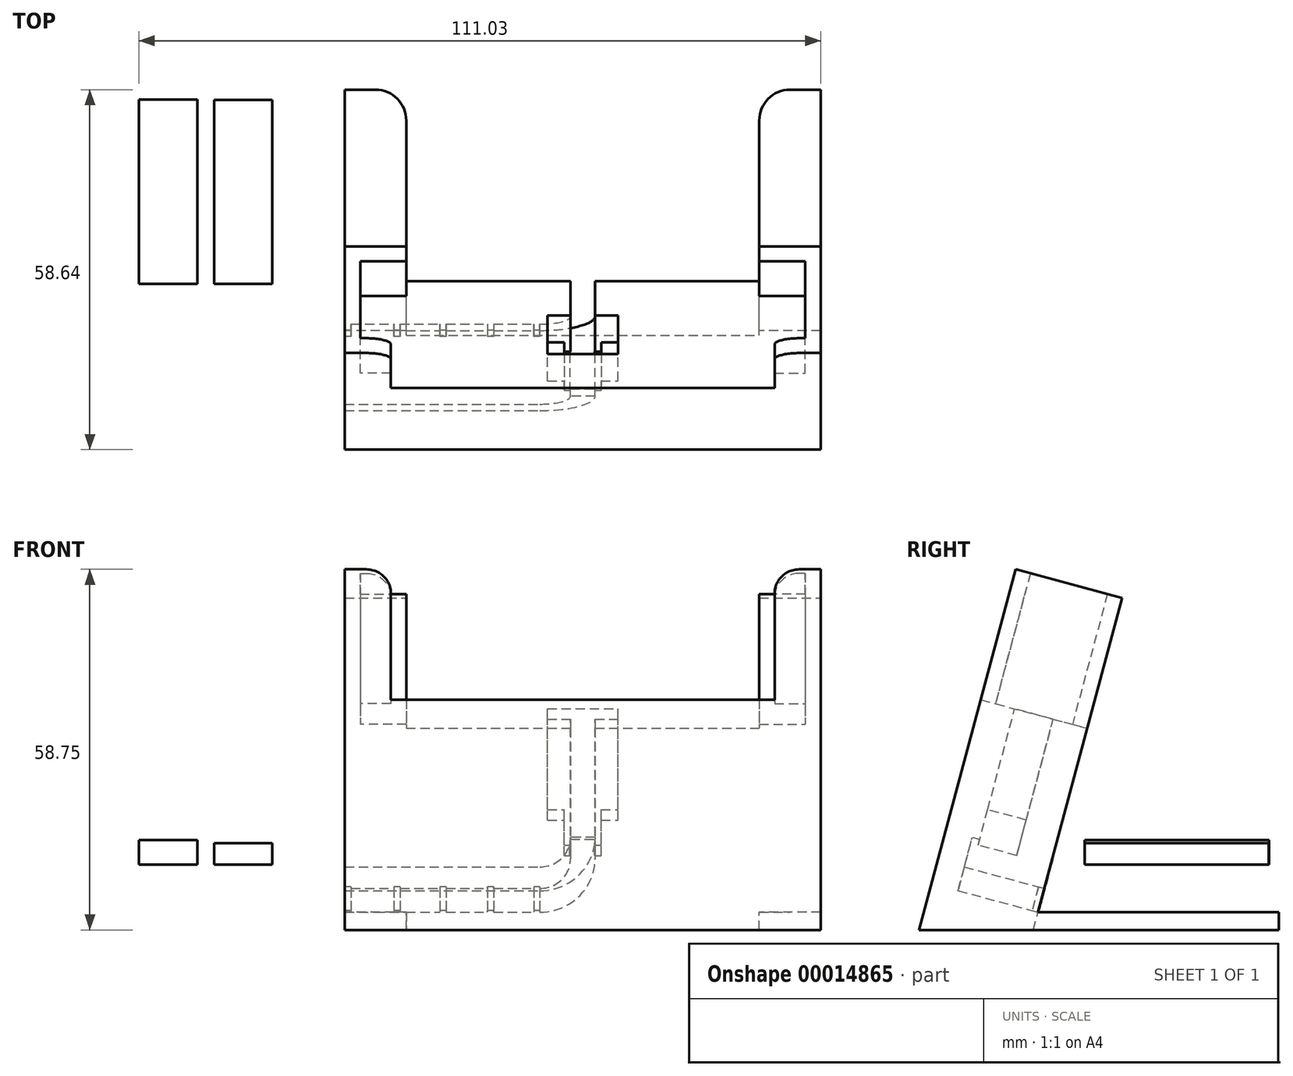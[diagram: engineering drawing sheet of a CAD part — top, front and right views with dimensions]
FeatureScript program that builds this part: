
annotation { "Feature Type Name" : "Feature", "Feature Type Description" : "" }
export const myFeature = defineFeature(function(context is Context, id is Id, definition is map)
    precondition{}
    {
        {
            var Q0;
            Q0=qCreatedBy(makeId("Top.planeOp"),FACE);
            var sketch = newSketch(context, id + "F0", { "sketchPlane" : qUnion([Q0])});
            skLineSegment(sketch, "E0.bottom", {"start": v(0, 0) * mm, "end": v(77.5, 0) * mm});
            skLineSegment(sketch, "E0.top", {"start": v(0, -18) * mm, "end": v(77.5, -18) * mm});
            skLineSegment(sketch, "E0.left", {"start": v(0, 0) * mm, "end": v(0, -18) * mm});
            skLineSegment(sketch, "E0.right", {"start": v(77.5, 0) * mm, "end": v(77.5, -18) * mm});
            skSolve(sketch);
        }
        {
            var Q0;
            Q0 = qSketchRegion(id + "F0", true);
            var Q1;
            Q1 = qSketchRegion(id + "F4", true);
            var Q2;
            Q2 = qSketchRegion(id + "F2", true);
            extrude(context, id + "F1", {"entities" : qUnion([Q0, Q1, Q2]), "depth" : 3 * mm, "hasSecondDirection" : true, "secondDirectionOppositeDirection" : true, "secondDirectionDepth" : 31 * mm});
        }
        {
            var Q0;
            Q0=makeQuery(id+"F0.imprint","IMPRINT",FACE,{"disambiguationData":[TD([[makeQuery(id+"F0.imprint","IMPRINT",EDGE,{"derivedFrom":sQuery(id+"F0.wireOp",EDGE,"E0.bottom")}),-1.0]])]});
            var sketch = newSketch(context, id + "F2", { "sketchPlane" : qUnion([Q0])});
            skLineSegment(sketch, "E1.bottom", {"start": v(0, 0) * mm, "end": v(10, 0) * mm});
            skLineSegment(sketch, "E1.top", {"start": v(0, -2.5) * mm, "end": v(10, -2.5) * mm});
            skLineSegment(sketch, "E1.left", {"start": v(0, 0) * mm, "end": v(0, -2.5) * mm});
            skLineSegment(sketch, "E1.right", {"start": v(10, 0) * mm, "end": v(10, -2.5) * mm});
            skLineSegment(sketch, "E2.bottom", {"start": v(0, -2.5) * mm, "end": v(2.5, -2.5) * mm});
            skLineSegment(sketch, "E2.top", {"start": v(0, -18) * mm, "end": v(2.5, -18) * mm});
            skLineSegment(sketch, "E2.left", {"start": v(0, -2.5) * mm, "end": v(0, -18) * mm});
            skLineSegment(sketch, "E2.right", {"start": v(2.5, -2.5) * mm, "end": v(2.5, -18) * mm});
            skLineSegment(sketch, "E3.bottom", {"start": v(2.5, -15.5) * mm, "end": v(7.5, -15.5) * mm});
            skLineSegment(sketch, "E3.top", {"start": v(2.5, -18) * mm, "end": v(7.5, -18) * mm});
            skLineSegment(sketch, "E3.left", {"start": v(2.5, -15.5) * mm, "end": v(2.5, -18) * mm});
            skLineSegment(sketch, "E3.right", {"start": v(7.5, -15.5) * mm, "end": v(7.5, -18) * mm});
            skLineSegment(sketch, "E4", {"start": v(38.75, 38.6) * mm, "end": v(38.75, -47.5) * mm});
            skLineSegment(sketch, "E5.0.MirrorCS", {"start": v(77.5, -2.5) * mm, "end": v(75, -2.5) * mm});
            skLineSegment(sketch, "E5.1.MirrorCS", {"start": v(77.5, -18) * mm, "end": v(75, -18) * mm});
            skLineSegment(sketch, "E5.2.MirrorCS", {"start": v(67.5, 0) * mm, "end": v(67.5, -2.5) * mm});
            skLineSegment(sketch, "E5.3.MirrorCS", {"start": v(77.5, 0) * mm, "end": v(77.5, -2.5) * mm});
            skLineSegment(sketch, "E5.4.MirrorCS", {"start": v(75, -15.5) * mm, "end": v(75, -18) * mm});
            skLineSegment(sketch, "E5.5.MirrorCS", {"start": v(70, -15.5) * mm, "end": v(70, -18) * mm});
            skLineSegment(sketch, "E5.6.MirrorCS", {"start": v(77.5, -2.5) * mm, "end": v(77.5, -18) * mm});
            skLineSegment(sketch, "E5.7.MirrorCS", {"start": v(77.5, 0) * mm, "end": v(67.5, 0) * mm});
            skLineSegment(sketch, "E5.8.MirrorCS", {"start": v(77.5, -2.5) * mm, "end": v(67.5, -2.5) * mm});
            skLineSegment(sketch, "E5.9.MirrorCS", {"start": v(75, -2.5) * mm, "end": v(75, -18) * mm});
            skLineSegment(sketch, "E5.10.MirrorCS", {"start": v(75, -18) * mm, "end": v(70, -18) * mm});
            skLineSegment(sketch, "E5.11.MirrorCS", {"start": v(75, -15.5) * mm, "end": v(70, -15.5) * mm});
            skSolve(sketch);
        }
        {
            var Q0;
            Q0 = qSketchRegion(id + "F2", true);
            var Q1;
            Q1 = qSketchRegion(id + "F4", true);
            extrude(context, id + "F3", {"entities" : qUnion([Q0, Q1]), "operationType" : NewBodyOperationType.ADD, "depth" : 25 * mm});
        }
        {
            var Q0;
            Q0=makeQuery(id+"F1.opExtrude","CAP_FACE",FACE,{"disambiguationData":[OSD([sQuery(id+"F0.wireOp",EDGE,"E0.bottom"),sQuery(id+"F0.wireOp",EDGE,"E0.top"),sQuery(id+"F0.wireOp",EDGE,"E0.left"),sQuery(id+"F0.wireOp",EDGE,"E0.right")])],"isStart":false});
            var sketch = newSketch(context, id + "F4", { "sketchPlane" : qUnion([Q0])});
            skLineSegment(sketch, "E6.bottom", {"start": v(33, -5.75) * mm, "end": v(44.5, -5.75) * mm});
            skLineSegment(sketch, "E6.top", {"start": v(33, -12.25) * mm, "end": v(44.5, -12.25) * mm});
            skLineSegment(sketch, "E6.left", {"start": v(33, -5.75) * mm, "end": v(33, -12.25) * mm});
            skLineSegment(sketch, "E6.right", {"start": v(44.5, -5.75) * mm, "end": v(44.5, -12.25) * mm});
            skSolve(sketch);
        }
        {
            var Q0;
            Q0 = qSketchRegion(id + "F4", true);
            extrude(context, id + "F5", {"entities" : qUnion([Q0]), "operationType" : NewBodyOperationType.REMOVE, "oppositeDirection" : true, "depth" : 17 * mm});
        }
        {
            var Q0;
            Q0=makeQuery(id+"F5.boolean.opBoolean","COPY",FACE,{"derivedFrom":makeQuery(id+"F5.opExtrude","CAP_FACE",FACE,{"disambiguationData":[OSD([sQuery(id+"F4.wireOp",EDGE,"E6.bottom"),sQuery(id+"F4.wireOp",EDGE,"E6.top"),sQuery(id+"F4.wireOp",EDGE,"E6.left"),sQuery(id+"F4.wireOp",EDGE,"E6.right")])],"isStart":false})});
            var sketch = newSketch(context, id + "F6", { "sketchPlane" : qUnion([Q0])});
            skLineSegment(sketch, "E7.bottom", {"start": v(35.75, -5.75) * mm, "end": v(41.75, -5.75) * mm});
            skLineSegment(sketch, "E7.top", {"start": v(35.75, -12.25) * mm, "end": v(41.75, -12.25) * mm});
            skLineSegment(sketch, "E7.left", {"start": v(35.75, -5.75) * mm, "end": v(35.75, -12.25) * mm});
            skLineSegment(sketch, "E7.right", {"start": v(41.75, -5.75) * mm, "end": v(41.75, -12.25) * mm});
            skSolve(sketch);
        }
        {
            var Q0;
            Q0 = qSketchRegion(id + "F6", true);
            extrude(context, id + "F7", {"entities" : qUnion([Q0]), "operationType" : NewBodyOperationType.REMOVE, "oppositeDirection" : true, "depth" : 6 * mm});
        }
        {
            var Q0;
            Q0=makeQuery(id+"F3.boolean.opBoolean","MERGE",FACE,{"derivedFrom":[makeQuery(id+"F1.opExtrude","SWEPT_FACE",FACE,{"disambiguationData":[OSD([sQuery(id+"F0.wireOp",EDGE,"E0.bottom")])]}),makeQuery(id+"F3.opExtrude","SWEPT_FACE",FACE,{"disambiguationData":[OSD([sQuery(id+"F2.wireOp",EDGE,"E1.bottom")])]}),makeQuery(id+"F3.opExtrude","SWEPT_FACE",FACE,{"disambiguationData":[OSD([sQuery(id+"F2.wireOp",EDGE,"E5.7.MirrorCS")])]})]});
            var sketch = newSketch(context, id + "F8", { "sketchPlane" : qUnion([Q0])});
            skLineSegment(sketch, "E8.bottom", {"start": v(0, -28) * mm, "end": v(-31.75, -28) * mm});
            skLineSegment(sketch, "E8.top", {"start": v(0, -24) * mm, "end": v(-31.75, -24) * mm});
            skLineSegment(sketch, "E8.left", {"start": v(0, -28) * mm, "end": v(0, -24) * mm});
            skLineSegment(sketch, "E8.right", {"start": v(-31.75, -28) * mm, "end": v(-31.75, -24) * mm});
            skSolve(sketch);
        }
        {
            var Q0;
            Q0 = qSketchRegion(id + "F8", true);
            extrude(context, id + "F9", {"entities" : qUnion([Q0]), "operationType" : NewBodyOperationType.REMOVE, "oppositeDirection" : true, "depth" : 13.5 * mm});
        }
        {
            var Q0;
            Q0=makeQuery(id+"F3.boolean.opBoolean","MERGE",FACE,{"derivedFrom":[makeQuery(id+"F1.opExtrude","SWEPT_FACE",FACE,{"disambiguationData":[OSD([sQuery(id+"F0.wireOp",EDGE,"E0.top")])]}),makeQuery(id+"F3.opExtrude","SWEPT_FACE",FACE,{"disambiguationData":[OSD([sQuery(id+"F2.wireOp",EDGE,"E2.top"),sQuery(id+"F2.wireOp",EDGE,"E3.top")])]}),makeQuery(id+"F3.opExtrude","SWEPT_FACE",FACE,{"disambiguationData":[OSD([sQuery(id+"F2.wireOp",EDGE,"E5.1.MirrorCS"),sQuery(id+"F2.wireOp",EDGE,"E5.10.MirrorCS")])]})]});
            cPlane(context, id + "F10", {"entities" : qUnion([Q0]), "cplaneType" : CPlaneType.OFFSET, "offset" : 10 * mm, "oppositeDirection" : true, "width" : 150 * mm, "height" : 150 * mm});
        }
        {
            var Q0;
            Q0=qCreatedBy(makeId("Right.planeOp"),FACE);
            cPlane(context, id + "F11", {"entities" : qUnion([Q0]), "cplaneType" : CPlaneType.OFFSET, "offset" : 38.75 * mm, "width" : 150 * mm, "height" : 150 * mm});
        }
        {
            var Q0;
            Q0=makeQuery(id+"F1.opExtrude","CAP_FACE",FACE,{"disambiguationData":[OSD([sQuery(id+"F0.wireOp",EDGE,"E0.bottom"),sQuery(id+"F0.wireOp",EDGE,"E0.top"),sQuery(id+"F0.wireOp",EDGE,"E0.left"),sQuery(id+"F0.wireOp",EDGE,"E0.right")])],"isStart":false});
            cPlane(context, id + "F12", {"entities" : qUnion([Q0]), "cplaneType" : CPlaneType.OFFSET, "offset" : 34 * mm, "oppositeDirection" : true, "width" : 150 * mm, "height" : 150 * mm});
        }
        {
            var Q0;
            Q0=qCreatedBy(id+"F12.planeOp",FACE);
            cPlane(context, id + "F13", {"entities" : qUnion([Q0]), "cplaneType" : CPlaneType.OFFSET, "offset" : 6 * mm, "width" : 150 * mm, "height" : 150 * mm});
        }
        {
            var Q0;
            Q0=qCreatedBy(id+"F10.planeOp",FACE);
            var sketch = newSketch(context, id + "F14", { "sketchPlane" : qUnion([Q0])});
            skArc(sketch, "E9", {"start": v(31.75, -27) * mm, "mid": v(37.4, -24.66) * mm, "end": v(39.75, -19) * mm});
            skSolve(sketch);
        }
        {
            var Q0;
            Q0=makeQuery(id+"F9.boolean.opBoolean","COPY",FACE,{"derivedFrom":makeQuery(id+"F9.opExtrude","SWEPT_FACE",FACE,{"disambiguationData":[OSD([sQuery(id+"F8.wireOp",EDGE,"E8.right")])]})});
            var Q1;
            Q1=sQuery(id+"F14.wireOp",EDGE,"E9");
            sweep(context, id + "F15", {"operationType" : NewBodyOperationType.REMOVE, "profiles" : qUnion([Q0]), "path" : qUnion([Q1])});
        }
        {
            var Q0;
            Q0=makeQuery(id+"F3.boolean.opBoolean","MERGE",FACE,{"derivedFrom":[makeQuery(id+"F1.opExtrude","SWEPT_FACE",FACE,{"disambiguationData":[OSD([sQuery(id+"F0.wireOp",EDGE,"E0.bottom")])]}),makeQuery(id+"F3.opExtrude","SWEPT_FACE",FACE,{"disambiguationData":[OSD([sQuery(id+"F2.wireOp",EDGE,"E1.bottom")])]}),makeQuery(id+"F3.opExtrude","SWEPT_FACE",FACE,{"disambiguationData":[OSD([sQuery(id+"F2.wireOp",EDGE,"E5.7.MirrorCS")])]})]});
            var sketch = newSketch(context, id + "F16", { "sketchPlane" : qUnion([Q0])});
            skLineSegment(sketch, "E10.bottom", {"start": v(-40.75, 3) * mm, "end": v(-36.75, 3) * mm});
            skLineSegment(sketch, "E10.top", {"start": v(-40.75, -19) * mm, "end": v(-36.75, -19) * mm});
            skLineSegment(sketch, "E10.left", {"start": v(-40.75, 3) * mm, "end": v(-40.75, -19) * mm});
            skLineSegment(sketch, "E10.right", {"start": v(-36.75, 3) * mm, "end": v(-36.75, -19) * mm});
            skSolve(sketch);
        }
        {
            var Q0;
            Q0 = qSketchRegion(id + "F16", true);
            extrude(context, id + "F17", {"entities" : qUnion([Q0]), "operationType" : NewBodyOperationType.REMOVE, "oppositeDirection" : true, "depth" : 7 * mm});
        }
        {
            var Q0;
            Q0=makeQuery(id+"F1.opExtrude","SWEPT_BODY",BODY,{"disambiguationData":[OSD([sQuery(id+"F0.wireOp",EDGE,"E0.bottom"),sQuery(id+"F0.wireOp",EDGE,"E0.top"),sQuery(id+"F0.wireOp",EDGE,"E0.left"),sQuery(id+"F0.wireOp",EDGE,"E0.right")])]});
            var Q1;
            Q1=makeQuery(id+"F1.opExtrude","CAP_EDGE",EDGE,{"disambiguationData":[OSD([sQuery(id+"F0.wireOp",EDGE,"E0.top")])],"isStart":true});
            transform(context, id + "F18", {"entities" : qUnion([Q0]), "transformType" : TransformType.ROTATION, "transformAxis" : qUnion([Q1]), "angle" : 15 * degree, "oppositeDirection" : true, "makeCopy" : false});
        }
        {
            var Q0;
            Q0=makeQuery(id+"F3.boolean.opBoolean","MERGE",FACE,{"derivedFrom":[makeQuery(id+"F1.opExtrude","SWEPT_FACE",FACE,{"disambiguationData":[OSD([sQuery(id+"F0.wireOp",EDGE,"E0.right")])]}),makeQuery(id+"F3.opExtrude","SWEPT_FACE",FACE,{"disambiguationData":[OSD([sQuery(id+"F2.wireOp",EDGE,"E5.3.MirrorCS"),sQuery(id+"F2.wireOp",EDGE,"E5.6.MirrorCS")])]})]});
            var sketch = newSketch(context, id + "F19", { "sketchPlane" : qUnion([Q0])});
            skLineSegment(sketch, "E11", {"start": v(-18, -31) * mm, "end": v(-19.25, -35.66) * mm});
            skLineSegment(sketch, "E12", {"start": v(-19.25, -35.66) * mm, "end": v(-0.61, -35.66) * mm});
            skLineSegment(sketch, "E13", {"start": v(-0.61, -35.66) * mm, "end": v(-18, -31) * mm});
            skSolve(sketch);
        }
        {
            var Q0;
            Q0=makeQuery(id+"F19.imprint","IMPRINT",FACE,{"disambiguationData":[TD([[makeQuery(id+"F19.imprint","IMPRINT",EDGE,{"derivedFrom":sQuery(id+"F19.wireOp",EDGE,"E11")}),1.0]])]});
            extrude(context, id + "F20", {"entities" : qUnion([Q0]), "operationType" : NewBodyOperationType.ADD, "oppositeDirection" : true, "depth" : 77.5 * mm});
        }
        {
            var Q0;
            Q0=makeQuery(id+"F20.opExtrude","SWEPT_FACE",FACE,{"disambiguationData":[OSD([sQuery(id+"F19.wireOp",EDGE,"E12")])]});
            var sketch = newSketch(context, id + "F21", { "sketchPlane" : qUnion([Q0])});
            skLineSegment(sketch, "E14.bottom", {"start": v(0, 0.61) * mm, "end": v(10, 0.61) * mm});
            skLineSegment(sketch, "E14.top", {"start": v(0, -39.39) * mm, "end": v(10, -39.39) * mm});
            skLineSegment(sketch, "E14.left", {"start": v(0, 0.61) * mm, "end": v(0, -39.39) * mm});
            skLineSegment(sketch, "E14.right", {"start": v(10, 0.61) * mm, "end": v(10, -39.39) * mm});
            skLineSegment(sketch, "E15.MirrorCS", {"start": v(77.5, 0.61) * mm, "end": v(77.5, -39.39) * mm});
            skLineSegment(sketch, "E16.MirrorCS", {"start": v(67.5, 0.61) * mm, "end": v(67.5, -39.39) * mm});
            skLineSegment(sketch, "E17.MirrorCS", {"start": v(77.5, -39.39) * mm, "end": v(67.5, -39.39) * mm});
            skLineSegment(sketch, "E18.MirrorCS", {"start": v(77.5, 0.61) * mm, "end": v(67.5, 0.61) * mm});
            skSolve(sketch);
        }
        {
            var Q0;
            Q0 = qSketchRegion(id + "F21", true);
            extrude(context, id + "F22", {"entities" : qUnion([Q0]), "operationType" : NewBodyOperationType.ADD, "oppositeDirection" : true, "depth" : 2.9 * mm});
        }
        {
            var Q0;
            Q0=makeQuery(id+"F3.opExtrude","CAP_EDGE",EDGE,{"disambiguationData":[OSD([sQuery(id+"F2.wireOp",EDGE,"E3.right")])],"isStart":false});
            fillet(context, id + "F23", {"entities" : qUnion([Q0]), "radius" : 4 * mm, "tangentPropagation" : true, "allowEdgeOverflow" : false});
        }
        {
            var Q0;
            Q0=makeQuery(id+"F3.opExtrude","CAP_EDGE",EDGE,{"disambiguationData":[OSD([sQuery(id+"F2.wireOp",EDGE,"E5.5.MirrorCS")])],"isStart":false});
            fillet(context, id + "F24", {"entities" : qUnion([Q0]), "radius" : 4 * mm, "tangentPropagation" : true, "allowEdgeOverflow" : false});
        }
        {
            var Q0;
            Q0=makeQuery(id+"F22.opExtrude","SWEPT_EDGE",EDGE,{"disambiguationData":[OSD([sQuery(id+"F21.wireOp",EDGE,"E14.top"),sQuery(id+"F21.wireOp",EDGE,"E14.right")])]});
            fillet(context, id + "F25", {"entities" : qUnion([Q0]), "radius" : 5 * mm, "tangentPropagation" : true, "allowEdgeOverflow" : false});
        }
        {
            var Q0;
            Q0=makeQuery(id+"F22.opExtrude","SWEPT_EDGE",EDGE,{"disambiguationData":[OSD([sQuery(id+"F21.wireOp",EDGE,"E16.MirrorCS"),sQuery(id+"F21.wireOp",EDGE,"E17.MirrorCS")])]});
            fillet(context, id + "F26", {"entities" : qUnion([Q0]), "radius" : 5 * mm, "tangentPropagation" : true, "allowEdgeOverflow" : false});
        }
        {
            var Q0;
            Q0=makeQuery(id+"F9.boolean.opBoolean","COPY",FACE,{"derivedFrom":makeQuery(id+"F9.opExtrude","SWEPT_FACE",FACE,{"disambiguationData":[OSD([sQuery(id+"F8.wireOp",EDGE,"E8.bottom")])]})});
            var sketch = newSketch(context, id + "F27", { "sketchPlane" : qUnion([Q0])});
            skLineSegment(sketch, "E19.bottom", {"start": v(1, 7.63) * mm, "end": v(0, 7.63) * mm});
            skLineSegment(sketch, "E19.top", {"start": v(1, 8.63) * mm, "end": v(0, 8.63) * mm});
            skLineSegment(sketch, "E19.left", {"start": v(1, 7.63) * mm, "end": v(1, 8.63) * mm});
            skLineSegment(sketch, "E19.right", {"start": v(0, 7.63) * mm, "end": v(0, 8.63) * mm});
            skLineSegment(sketch, "E20.bottom", {"start": v(31.75, 7.64) * mm, "end": v(30.75, 7.64) * mm});
            skLineSegment(sketch, "E20.top", {"start": v(31.75, 8.64) * mm, "end": v(30.75, 8.64) * mm});
            skLineSegment(sketch, "E20.left", {"start": v(31.75, 7.64) * mm, "end": v(31.75, 8.64) * mm});
            skLineSegment(sketch, "E20.right", {"start": v(30.75, 7.64) * mm, "end": v(30.75, 8.64) * mm});
            skLineSegment(sketch, "E21.bottom", {"start": v(16.5, 7.64) * mm, "end": v(15.5, 7.64) * mm});
            skLineSegment(sketch, "E21.top", {"start": v(16.5, 8.64) * mm, "end": v(15.5, 8.64) * mm});
            skLineSegment(sketch, "E21.left", {"start": v(16.5, 7.64) * mm, "end": v(16.5, 8.64) * mm});
            skLineSegment(sketch, "E21.right", {"start": v(15.5, 7.64) * mm, "end": v(15.5, 8.64) * mm});
            skLineSegment(sketch, "E22.bottom", {"start": v(24.25, 8.64) * mm, "end": v(23.25, 8.64) * mm});
            skLineSegment(sketch, "E22.top", {"start": v(24.25, 7.64) * mm, "end": v(23.25, 7.64) * mm});
            skLineSegment(sketch, "E22.left", {"start": v(24.25, 8.64) * mm, "end": v(24.25, 7.64) * mm});
            skLineSegment(sketch, "E22.right", {"start": v(23.25, 8.64) * mm, "end": v(23.25, 7.64) * mm});
            skLineSegment(sketch, "E23.bottom", {"start": v(9, 7.63) * mm, "end": v(8, 7.63) * mm});
            skLineSegment(sketch, "E23.top", {"start": v(9, 8.63) * mm, "end": v(8, 8.63) * mm});
            skLineSegment(sketch, "E23.left", {"start": v(9, 7.63) * mm, "end": v(9, 8.63) * mm});
            skLineSegment(sketch, "E23.right", {"start": v(8, 7.63) * mm, "end": v(8, 8.63) * mm});
            skSolve(sketch);
        }
        {
            var Q0;
            Q0 = qSketchRegion(id + "F27", true);
            extrude(context, id + "F28", {"entities" : qUnion([Q0]), "operationType" : NewBodyOperationType.ADD, "depth" : 4 * mm});
        }
        {
            var Q0;
            Q0=qCreatedBy(id+"F13.planeOp",FACE);
            var sketch = newSketch(context, id + "F29", { "sketchPlane" : qUnion([Q0])});
            skLineSegment(sketch, "E24.bottom", {"start": v(-21.3, 37.74) * mm, "end": v(-11.8, 37.74) * mm});
            skLineSegment(sketch, "E24.top", {"start": v(-21.3, 7.74) * mm, "end": v(-11.8, 7.74) * mm});
            skLineSegment(sketch, "E24.left", {"start": v(-21.3, 37.74) * mm, "end": v(-21.3, 7.74) * mm});
            skLineSegment(sketch, "E24.right", {"start": v(-11.8, 37.74) * mm, "end": v(-11.8, 7.74) * mm});
            skSolve(sketch);
        }
        {
            var Q0;
            Q0 = qSketchRegion(id + "F29", true);
            extrude(context, id + "F30", {"entities" : qUnion([Q0]), "depth" : 3.5 * mm});
        }
        {
            var Q0;
            Q0=qCreatedBy(id+"F13.planeOp",FACE);
            var sketch = newSketch(context, id + "F31", { "sketchPlane" : qUnion([Q0])});
            skLineSegment(sketch, "E25.bottom", {"start": v(-24.03, 7.78) * mm, "end": v(-33.53, 7.78) * mm});
            skLineSegment(sketch, "E25.top", {"start": v(-24.03, 37.78) * mm, "end": v(-33.53, 37.78) * mm});
            skLineSegment(sketch, "E25.left", {"start": v(-24.03, 7.78) * mm, "end": v(-24.03, 37.78) * mm});
            skLineSegment(sketch, "E25.right", {"start": v(-33.53, 7.78) * mm, "end": v(-33.53, 37.78) * mm});
            skSolve(sketch);
        }
        {
            var Q0;
            Q0 = qSketchRegion(id + "F31", true);
            extrude(context, id + "F32", {"entities" : qUnion([Q0]), "depth" : 4 * mm});
        }
    });
